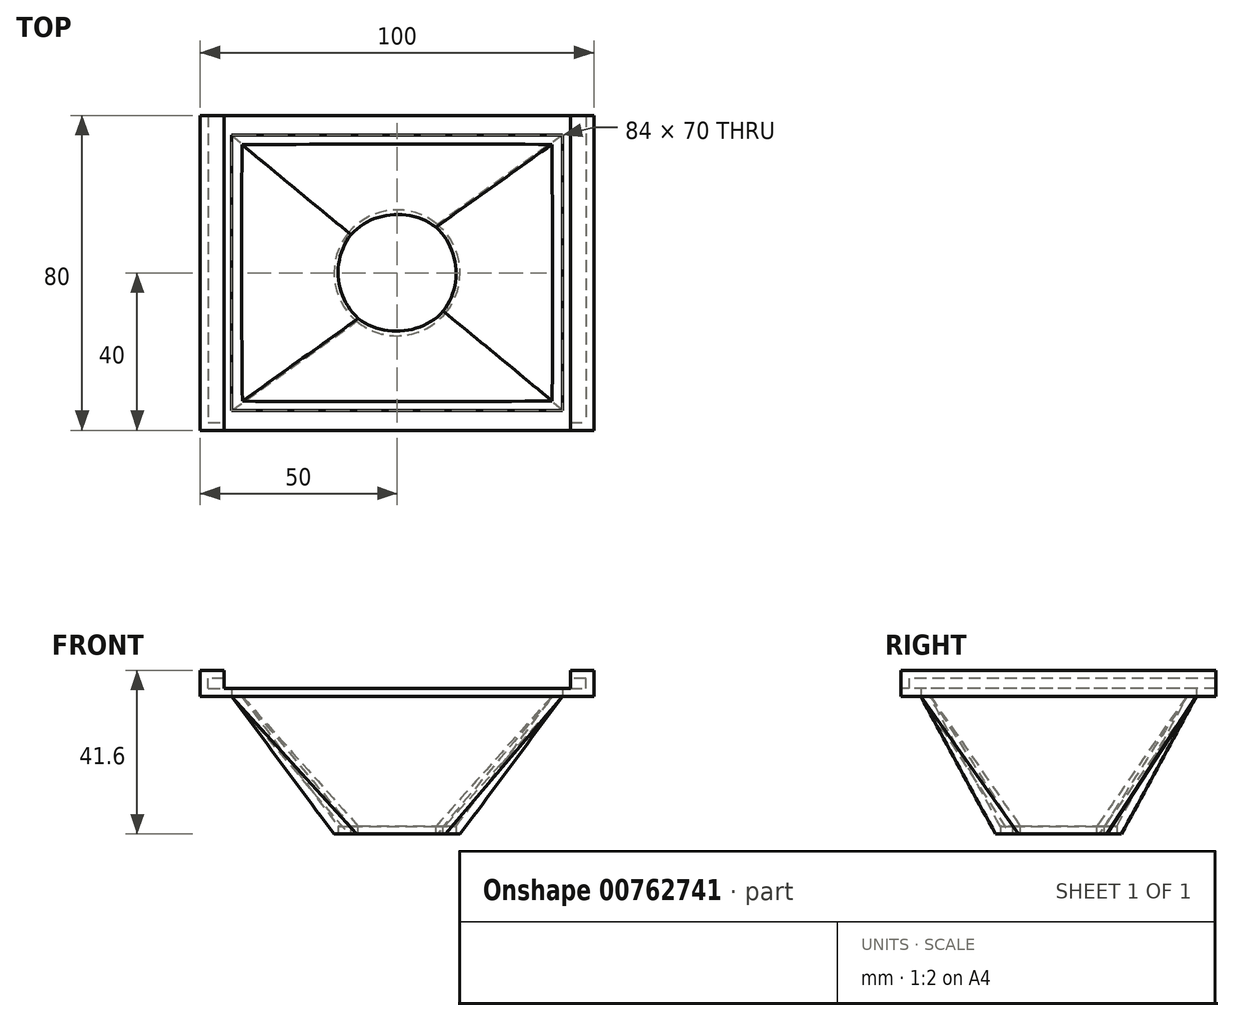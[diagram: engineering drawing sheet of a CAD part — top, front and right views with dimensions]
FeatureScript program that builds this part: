
annotation { "Feature Type Name" : "Feature", "Feature Type Description" : "" }
export const myFeature = defineFeature(function(context is Context, id is Id, definition is map)
    precondition{}
    {
        {
            var Q0;
            Q0=qCreatedBy(makeId("Top.planeOp"),FACE);
            var sketch = newSketch(context, id + "F0", { "sketchPlane" : qUnion([Q0])});
            skCircle(sketch, "E0", {"center": v(0, 0) * mm, "radius": 16 * mm});
            skSolve(sketch);
        }
        {
            var Q0;
            Q0=qCreatedBy(makeId("Top.planeOp"),FACE);
            cPlane(context, id + "F1", {"entities" : qUnion([Q0]), "cplaneType" : CPlaneType.OFFSET, "offset" : 35 * mm, "width" : 150 * mm, "height" : 150 * mm});
        }
        {
            var Q0;
            Q0=qCreatedBy(id+"F1.planeOp",FACE);
            var sketch = newSketch(context, id + "F2", { "sketchPlane" : qUnion([Q0])});
            skLineSegment(sketch, "E1.bottom", {"start": v(-50, 40) * mm, "end": v(50, 40) * mm});
            skLineSegment(sketch, "E1.top", {"start": v(-50, -40) * mm, "end": v(50, -40) * mm});
            skLineSegment(sketch, "E1.left", {"start": v(-50, 40) * mm, "end": v(-50, -40) * mm});
            skLineSegment(sketch, "E1.right", {"start": v(50, 40) * mm, "end": v(50, -40) * mm});
            skLineSegment(sketch, "E2.bottom", {"start": v(-42, 35) * mm, "end": v(42, 35) * mm});
            skLineSegment(sketch, "E2.top", {"start": v(-42, -35) * mm, "end": v(42, -35) * mm});
            skLineSegment(sketch, "E2.left", {"start": v(-42, 35) * mm, "end": v(-42, -35) * mm});
            skLineSegment(sketch, "E2.right", {"start": v(42, 35) * mm, "end": v(42, -35) * mm});
            skSolve(sketch);
        }
        {
            var Q0;
            Q0=makeQuery(id+"F2.imprint","IMPRINT",FACE,{"disambiguationData":[TD([[makeQuery(id+"F2.imprint","IMPRINT",EDGE,{"derivedFrom":sQuery(id+"F2.wireOp",EDGE,"E2.bottom")}),-1.0]])]});
            var Q1;
            Q1=makeQuery(id+"F0.imprint","IMPRINT",FACE,{"disambiguationData":[TD([[makeQuery(id+"F0.imprint","IMPRINT",EDGE,{"derivedFrom":sQuery(id+"F0.wireOp",EDGE,"E0")}),1.0]])]});
            var Q2;
            Q2=makeQuery(id+"F2.imprint","IMPRINT",FACE,{"disambiguationData":[TD([[makeQuery(id+"F2.imprint","IMPRINT",EDGE,{"derivedFrom":sQuery(id+"F2.wireOp",EDGE,"VucVfbho-iUvj-7R6x-qe9E-N3hCGbcbC73Y")}),1.0]])]});
            var Q3;
            Q3=makeQuery(id+"F0.imprint","IMPRINT",FACE,{"disambiguationData":[TD([[makeQuery(id+"F0.imprint","IMPRINT",EDGE,{"derivedFrom":sQuery(id+"F0.wireOp",EDGE,"E0")}),1.0]])]});
            loft(context, id + "F3", {"sheetProfilesArray" : [{ "sheetProfileEntities" : qUnion([Q0]) }, { "sheetProfileEntities" : qUnion([Q1]) }], "wireProfilesArray" : [{ "wireProfileEntities" : qUnion([Q2]) }, { "wireProfileEntities" : qUnion([Q3]) }]});
        }
        {
            var Q0;
            Q0=makeQuery(id+"F3.opLoft","CAP_FACE",FACE,{"disambiguationData":[OSD([makeQuery(id+"F2.imprint","IMPRINT",FACE,{"disambiguationData":[TD([[makeQuery(id+"F2.imprint","IMPRINT",EDGE,{"derivedFrom":sQuery(id+"F2.wireOp",EDGE,"E2.bottom")}),-1.0]])]})])],"isStart":true});
            shell(context, id + "F4", {"entities" : qUnion([Q0]), "thickness" : 2 * mm});
        }
        {
            var Q0;
            Q0 = qSketchRegion(id + "F2", true);
            extrude(context, id + "F5", {"entities" : qUnion([Q0]), "depth" : 2 * mm, "offsetDistance" : 25 * mm});
        }
        {
            var Q0;
            Q0=makeQuery(id+"F5.opExtrude","CAP_FACE",FACE,{"disambiguationData":[OSD([sQuery(id+"F2.wireOp",EDGE,"VucVfbho-iUvj-7R6x-qe9E-N3hCGbcbC73Y"),sQuery(id+"F2.wireOp",EDGE,"E1.bottom"),sQuery(id+"F2.wireOp",EDGE,"E1.top"),sQuery(id+"F2.wireOp",EDGE,"E1.left"),sQuery(id+"F2.wireOp",EDGE,"E1.right")])],"isStart":false});
            var sketch = newSketch(context, id + "F6", { "sketchPlane" : qUnion([Q0])});
            skLineSegment(sketch, "E3.bottom", {"start": v(-50, 40) * mm, "end": v(-44, 40) * mm});
            skLineSegment(sketch, "E3.top", {"start": v(-50, -40) * mm, "end": v(-44, -40) * mm});
            skLineSegment(sketch, "E3.left", {"start": v(-50, 40) * mm, "end": v(-50, -40) * mm});
            skLineSegment(sketch, "E3.right", {"start": v(-44, 40) * mm, "end": v(-44, -40) * mm});
            skLineSegment(sketch, "E4.MirrorCS", {"start": v(44, 40) * mm, "end": v(44, -40) * mm});
            skLineSegment(sketch, "E5.MirrorCS", {"start": v(50, 40) * mm, "end": v(44, 40) * mm});
            skLineSegment(sketch, "E6.MirrorCS", {"start": v(50, 40) * mm, "end": v(50, -40) * mm});
            skLineSegment(sketch, "E7.MirrorCS", {"start": v(50, -40) * mm, "end": v(44, -40) * mm});
            skSolve(sketch);
        }
        {
            var Q0;
            Q0=makeQuery(id+"F6.imprint","IMPRINT",FACE,{"disambiguationData":[TD([[makeQuery(id+"F6.imprint","IMPRINT",EDGE,{"derivedFrom":sQuery(id+"F6.wireOp",EDGE,"E3.bottom")}),-1.0]])]});
            var Q1;
            Q1=makeQuery(id+"F6.imprint","IMPRINT",FACE,{"disambiguationData":[TD([[makeQuery(id+"F6.imprint","IMPRINT",EDGE,{"derivedFrom":sQuery(id+"F6.wireOp",EDGE,"E4.MirrorCS")}),1.0]])]});
            extrude(context, id + "F7", {"entities" : qUnion([Q0, Q1]), "operationType" : NewBodyOperationType.ADD, "depth" : 4.6 * mm, "offsetDistance" : 25 * mm});
        }
        {
            var Q0;
            Q0=makeQuery(id+"F7.opExtrude","SWEPT_FACE",FACE,{"disambiguationData":[OSD([sQuery(id+"F6.wireOp",EDGE,"E3.right")])]});
            var Q1;
            Q1=makeQuery(id+"F7.opExtrude","SWEPT_FACE",FACE,{"disambiguationData":[OSD([sQuery(id+"F6.wireOp",EDGE,"E4.MirrorCS")])]});
            shell(context, id + "F8", {"entities" : qUnion([Q0, Q1]), "thickness" : 2 * mm});
        }
        {
            var Q0;
            Q0=makeQuery(id+"F8.opShell","OFFSET_FACE",FACE,{"disambiguationData":[OSD([sQuery(id+"F2.wireOp",EDGE,"E1.bottom"),sQuery(id+"F6.wireOp",EDGE,"E3.bottom"),sQuery(id+"F6.wireOp",EDGE,"E5.MirrorCS")]),OD(0.0)]});
            var Q1;
            Q1=makeQuery(id+"F8.opShell","OFFSET_FACE",FACE,{"disambiguationData":[OSD([sQuery(id+"F2.wireOp",EDGE,"E1.bottom"),sQuery(id+"F6.wireOp",EDGE,"E3.bottom"),sQuery(id+"F6.wireOp",EDGE,"E5.MirrorCS")]),OD(1.0)]});
            extrude(context, id + "F9", {"entities" : qUnion([Q0, Q1]), "operationType" : NewBodyOperationType.REMOVE, "oppositeDirection" : true, "depth" : 3 * mm, "offsetDistance" : 25 * mm});
        }
        {
            var Q0;
            Q0=makeQuery(id+"F4.opShell","OFFSET_FACE",FACE,{"disambiguationData":[OSD([makeQuery(id+"F0.imprint","IMPRINT",FACE,{"disambiguationData":[TD([[makeQuery(id+"F0.imprint","IMPRINT",EDGE,{"derivedFrom":sQuery(id+"F0.wireOp",EDGE,"E0")}),1.0]])]})])]});
            extrude(context, id + "F10", {"entities" : qUnion([Q0]), "operationType" : NewBodyOperationType.REMOVE, "oppositeDirection" : true, "depth" : 2 * mm, "offsetDistance" : 25 * mm});
        }
    });
